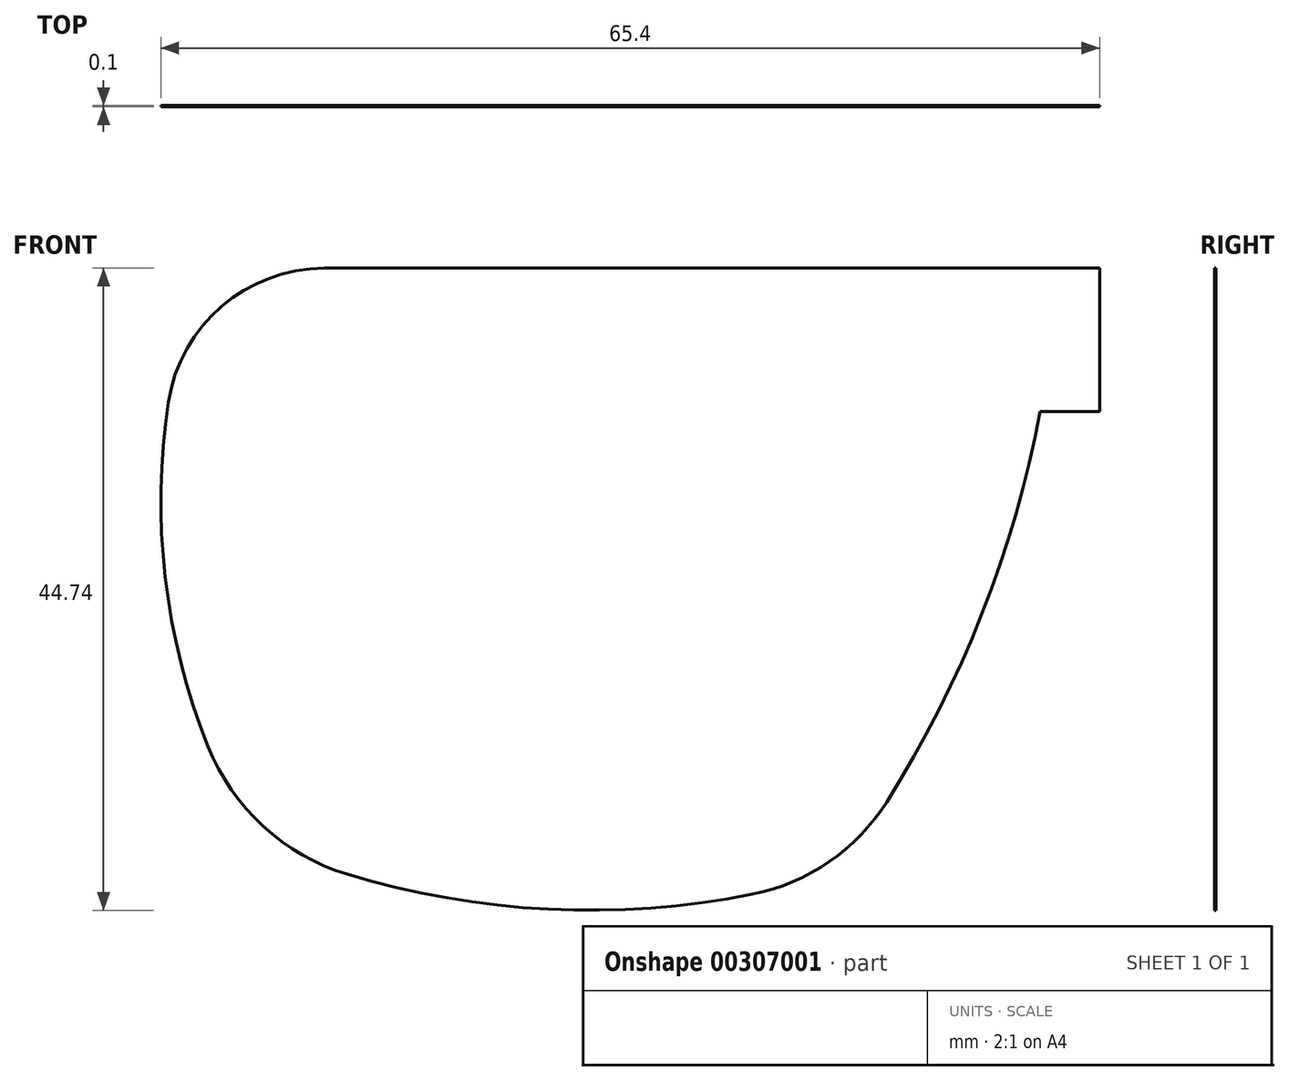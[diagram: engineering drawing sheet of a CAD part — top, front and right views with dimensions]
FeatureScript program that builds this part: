
annotation { "Feature Type Name" : "Feature", "Feature Type Description" : "" }
export const myFeature = defineFeature(function(context is Context, id is Id, definition is map)
    precondition{}
    {
        {
            var Q0;
            Q0=qCreatedBy(makeId("Front.planeOp"),FACE);
            var sketch = newSketch(context, id + "F0", { "sketchPlane" : qUnion([Q0])});
            skLineSegment(sketch, "E0", {"start": v(0, 0) * mm, "end": v(-56, 0) * mm, "construction": true});
            skLineSegment(sketch, "E1", {"start": v(0, 0) * mm, "end": v(0, -14) * mm, "construction": true});
            skLineSegment(sketch, "E2", {"start": v(-4.5, -14) * mm, "end": v(0, -14) * mm, "construction": true});
            skArc(sketch, "E3", {"start": v(-68.85, -11.04) * mm, "mid": v(-69.09, -23.75) * mm, "end": v(-65.97, -36.07) * mm, "construction": true});
            skArc(sketch, "E4", {"start": v(-55.01, -46.13) * mm, "mid": v(-40.5, -48.67) * mm, "end": v(-25.8, -47.58) * mm, "construction": true});
            skArc(sketch, "E5", {"start": v(-15.13, -40.25) * mm, "mid": v(-8.64, -27.6) * mm, "end": v(-4.5, -14) * mm, "construction": true});
            skArc(sketch, "E6", {"start": v(-56, 0) * mm, "mid": v(-64.47, -3.14) * mm, "end": v(-68.85, -11.04) * mm, "construction": true});
            skArc(sketch, "E7", {"start": v(-65.97, -36.07) * mm, "mid": v(-61.63, -42.35) * mm, "end": v(-55.01, -46.13) * mm, "construction": true});
            skArc(sketch, "E8", {"start": v(-25.8, -47.58) * mm, "mid": v(-19.7, -45.01) * mm, "end": v(-15.13, -40.25) * mm, "construction": true});
            skArc(sketch, "E9.0", {"start": v(-66.87, -11.34) * mm, "mid": v(-67.1, -23.52) * mm, "end": v(-64.11, -35.33) * mm});
            skArc(sketch, "E9.1", {"start": v(-56, -2) * mm, "mid": v(-63.17, -4.66) * mm, "end": v(-66.87, -11.34) * mm});
            skArc(sketch, "E9.2", {"start": v(-64.11, -35.33) * mm, "mid": v(-60.28, -40.88) * mm, "end": v(-54.43, -44.22) * mm});
            skLineSegment(sketch, "E9.3", {"start": v(-2, -2) * mm, "end": v(-56, -2) * mm});
            skLineSegment(sketch, "E9.4", {"start": v(-2, -2) * mm, "end": v(-2, -12) * mm});
            skArc(sketch, "E9.5", {"start": v(-54.43, -44.22) * mm, "mid": v(-40.4, -46.67) * mm, "end": v(-26.19, -45.62) * mm});
            skArc(sketch, "E9.6", {"start": v(-26.19, -45.62) * mm, "mid": v(-20.84, -43.37) * mm, "end": v(-16.82, -39.18) * mm});
            skArc(sketch, "E9.7", {"start": v(-16.82, -39.18) * mm, "mid": v(-10.2, -26.1) * mm, "end": v(-6.14, -12) * mm});
            skLineSegment(sketch, "E9.8", {"start": v(-6.14, -12) * mm, "end": v(-2, -12) * mm});
            skSolve(sketch);
        }
        {
            var Q0;
            Q0=makeQuery(id+"F0.imprint","IMPRINT",FACE,{"disambiguationData":[TD([[makeQuery(id+"F0.imprint","IMPRINT",EDGE,{"derivedFrom":sQuery(id+"F0.wireOp",EDGE,"E9.0")}),1.0]])]});
            extrude(context, id + "F1", {"entities" : qUnion([Q0]), "oppositeDirection" : true, "depth" : 0.1 * mm});
        }
    });
